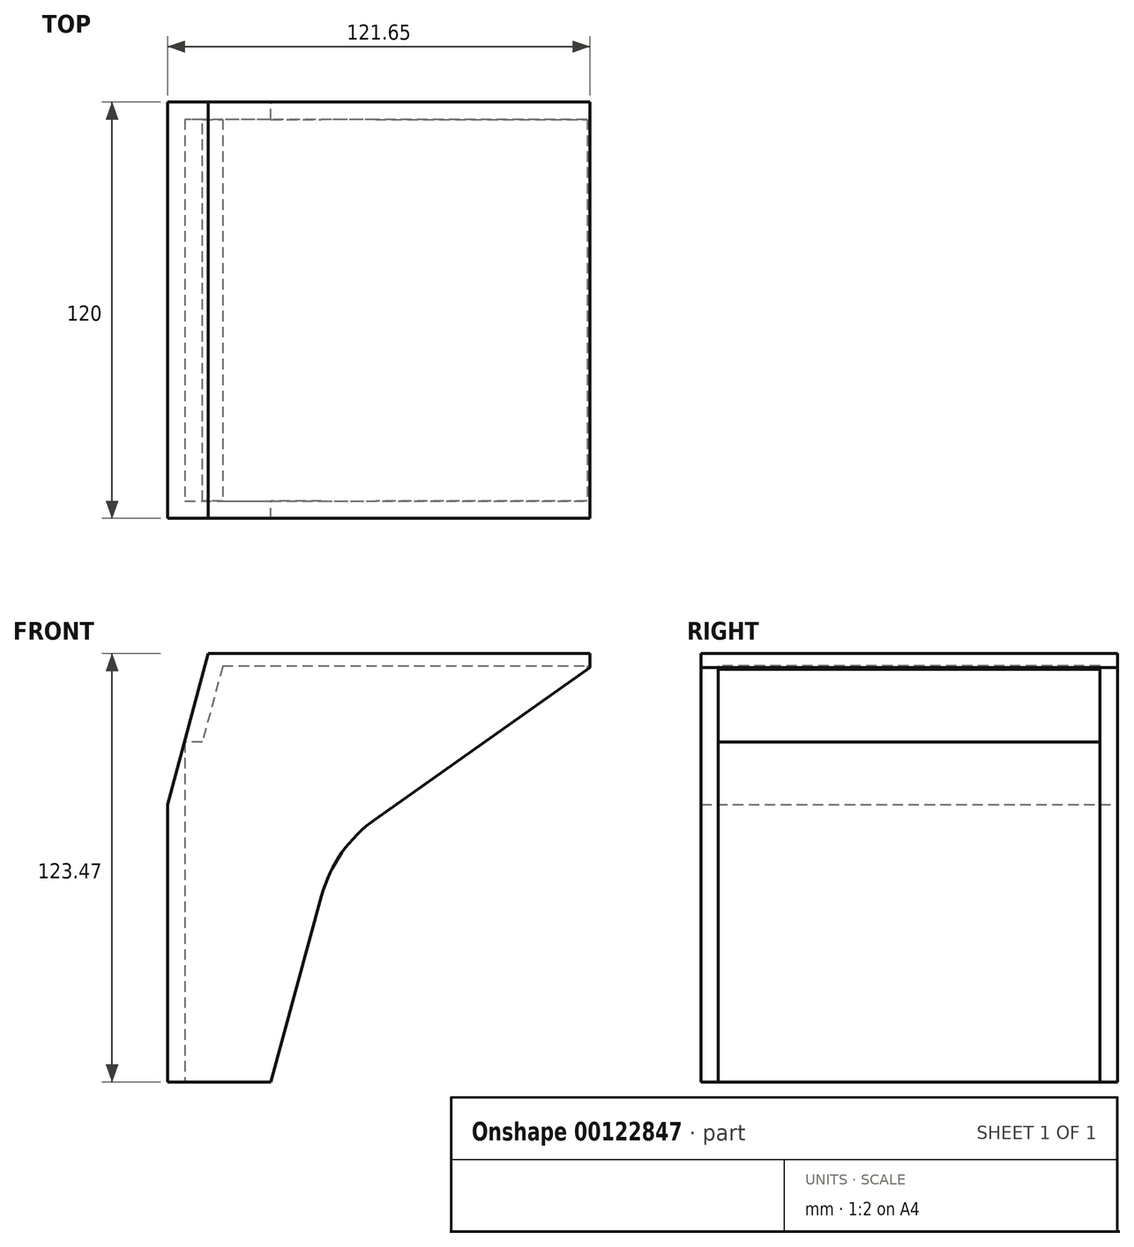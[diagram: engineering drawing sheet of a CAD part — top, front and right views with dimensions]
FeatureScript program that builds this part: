
annotation { "Feature Type Name" : "Feature", "Feature Type Description" : "" }
export const myFeature = defineFeature(function(context is Context, id is Id, definition is map)
    precondition{}
    {
        {
            var Q0;
            Q0=qCreatedBy(makeId("Front.planeOp"),FACE);
            var sketch = newSketch(context, id + "F0", { "sketchPlane" : qUnion([Q0])});
            skLineSegment(sketch, "E0", {"start": v(0, 0) * mm, "end": v(0, 80) * mm});
            skLineSegment(sketch, "E1", {"start": v(0, 80) * mm, "end": v(11.65, 123.47) * mm});
            skLineSegment(sketch, "E2", {"start": v(11.65, 123.47) * mm, "end": v(121.65, 123.47) * mm});
            skLineSegment(sketch, "E3", {"start": v(0, 0) * mm, "end": v(29.72, 0) * mm});
            skLineSegment(sketch, "E4", {"start": v(29.72, 0) * mm, "end": v(44.36, 53.68) * mm});
            skLineSegment(sketch, "E5", {"start": v(121.65, 123.47) * mm, "end": v(121.65, 119.47) * mm});
            skLineSegment(sketch, "E6", {"start": v(59.87, 75.82) * mm, "end": v(121.65, 119.47) * mm});
            skPoint(sketch, "E7.visualSharp", {"position": v(48.14, 67.53) * mm});
            skArc(sketch, "E7.filletArc", {"start": v(59.87, 75.82) * mm, "mid": v(50.2, 66.1) * mm, "end": v(44.36, 53.68) * mm});
            skSolve(sketch);
        }
        {
            var Q0;
            Q0=makeQuery(id+"F0.imprint","IMPRINT",FACE,{"disambiguationData":[TD([[makeQuery(id+"F0.imprint","IMPRINT",EDGE,{"derivedFrom":sQuery(id+"F0.wireOp",EDGE,"E0")}),-1.0]])]});
            extrude(context, id + "F1", {"entities" : qUnion([Q0]), "depth" : 120 * mm});
        }
        {
            var Q0;
            Q0=makeQuery(id+"F1.opExtrude","SWEPT_FACE",FACE,{"disambiguationData":[OSD([sQuery(id+"F0.wireOp",EDGE,"E3")])]});
            var sketch = newSketch(context, id + "F2", { "sketchPlane" : qUnion([Q0])});
            skLineSegment(sketch, "E8.0", {"start": v(0, 120) * mm, "end": v(0, 0) * mm, "construction": true});
            skLineSegment(sketch, "E9", {"start": v(0, 60) * mm, "end": v(5, 60) * mm, "construction": true});
            skLineSegment(sketch, "E10", {"start": v(5, 60) * mm, "end": v(5, 100) * mm});
            skLineSegment(sketch, "E11", {"start": v(5, 100) * mm, "end": v(115, 100) * mm});
            skLineSegment(sketch, "E12", {"start": v(115, 100) * mm, "end": v(115, 20) * mm});
            skLineSegment(sketch, "E13", {"start": v(115, 20) * mm, "end": v(5, 20) * mm});
            skLineSegment(sketch, "E14", {"start": v(5, 20) * mm, "end": v(5, 60) * mm});
            skSolve(sketch);
        }
        {
            var Q0;
            {var subQ0=sQuery(id+"F2.wireOp",EDGE,"E12");Q0=makeQuery(id+"F2.imprint","IMPRINT",FACE,{"disambiguationData":[TD([[makeQuery(id+"F2.imprint","IMPRINT",EDGE,{"derivedFrom":subQ0}),-1.0]])]});}
            var Q1;
            {var subQ5=sQuery(id+"F2.wireOp",EDGE,"E10");Q1=makeQuery(id+"F2.imprint","IMPRINT",FACE,{"disambiguationData":[TD([[makeQuery(id+"F2.imprint","IMPRINT",EDGE,{"derivedFrom":subQ5}),-1.0]])]});}
            extrude(context, id + "F3", {"entities" : qUnion([Q0, Q1]), "operationType" : NewBodyOperationType.REMOVE, "oppositeDirection" : true, "depth" : 98 * mm});
        }
        {
            var Q0;
            Q0=makeQuery(id+"F1.opExtrude","SWEPT_FACE",FACE,{"disambiguationData":[OSD([sQuery(id+"F0.wireOp",EDGE,"E1")])]});
            cPlane(context, id + "F4", {"entities" : qUnion([Q0]), "cplaneType" : CPlaneType.OFFSET, "offset" : 5 * mm, "oppositeDirection" : true, "width" : 150 * mm, "height" : 150 * mm});
        }
        {
            var Q0;
            Q0=qCreatedBy(id+"F4.planeOp",FACE);
            var sketch = newSketch(context, id + "F5", { "sketchPlane" : qUnion([Q0])});
            skLineSegment(sketch, "E15.0", {"start": v(120, 77.27) * mm, "end": v(120, 122.27) * mm, "construction": true});
            skLineSegment(sketch, "E16", {"start": v(120, 99.77) * mm, "end": v(115, 99.77) * mm, "construction": true});
            skLineSegment(sketch, "E17", {"start": v(115, 99.77) * mm, "end": v(115, 119.77) * mm});
            skLineSegment(sketch, "E18", {"start": v(115, 99.77) * mm, "end": v(115, 79.77) * mm});
            skLineSegment(sketch, "E19", {"start": v(115, 79.77) * mm, "end": v(35, 79.77) * mm});
            skLineSegment(sketch, "E20", {"start": v(35, 79.77) * mm, "end": v(35, 119.77) * mm});
            skLineSegment(sketch, "E21", {"start": v(35, 119.77) * mm, "end": v(115, 119.77) * mm});
            skSolve(sketch);
        }
        {
            var Q0;
            Q0 = qSketchRegion(id + "F5", true);
            extrude(context, id + "F6", {"entities" : qUnion([Q0]), "operationType" : NewBodyOperationType.REMOVE, "oppositeDirection" : true, "depth" : 80 * mm});
        }
        {
            var Q0;
            Q0=qCreatedBy(makeId("Top.planeOp"),FACE);
            var sketch = newSketch(context, id + "F7", { "sketchPlane" : qUnion([Q0])});
            skLineSegment(sketch, "E22.0", {"start": v(15.83, -35) * mm, "end": v(15.83, -115) * mm});
            skLineSegment(sketch, "E23", {"start": v(15.83, -115) * mm, "end": v(120.83, -115) * mm});
            skLineSegment(sketch, "E24", {"start": v(120.83, -115) * mm, "end": v(120.83, -35) * mm});
            skLineSegment(sketch, "E25", {"start": v(120.83, -35) * mm, "end": v(15.83, -35) * mm});
            skSolve(sketch);
        }
        {
            var Q0;
            Q0=makeQuery(id+"F7.imprint","IMPRINT",FACE,{"disambiguationData":[TD([[makeQuery(id+"F7.imprint","IMPRINT",EDGE,{"derivedFrom":sQuery(id+"F7.wireOp",EDGE,"E22.0")}),1.0]])]});
            extrude(context, id + "F8", {"entities" : qUnion([Q0]), "operationType" : NewBodyOperationType.REMOVE, "depth" : 120 * mm});
        }
        {
            var Q0;
            Q0=makeQuery(id+"F3.boolean.opBoolean","COPY",FACE,{"derivedFrom":makeQuery(id+"F3.opExtrude","SWEPT_FACE",FACE,{"disambiguationData":[OSD([sQuery(id+"F2.wireOp",EDGE,"E13")])]})});
            extrude(context, id + "F9", {"entities" : qUnion([Q0]), "operationType" : NewBodyOperationType.REMOVE, "oppositeDirection" : true, "depth" : 15 * mm});
        }
        {
            var Q0;
            Q0=makeQuery(id+"F8.boolean.opBoolean","MERGE",FACE,{"derivedFrom":[makeQuery(id+"F6.boolean.opBoolean","COPY",FACE,{"derivedFrom":makeQuery(id+"F6.opExtrude","SWEPT_FACE",FACE,{"disambiguationData":[OSD([sQuery(id+"F5.wireOp",EDGE,"E20")])]})}),makeQuery(id+"F8.opExtrude","SWEPT_FACE",FACE,{"disambiguationData":[OSD([sQuery(id+"F7.wireOp",EDGE,"E25")])]})]});
            extrude(context, id + "F10", {"entities" : qUnion([Q0]), "operationType" : NewBodyOperationType.REMOVE, "oppositeDirection" : true, "depth" : 30 * mm});
        }
        {
            var Q0;
            Q0=makeQuery(id+"F3.boolean.opBoolean","COPY",FACE,{"derivedFrom":makeQuery(id+"F3.opExtrude","SWEPT_FACE",FACE,{"disambiguationData":[OSD([sQuery(id+"F2.wireOp",EDGE,"E11")])]})});
            extrude(context, id + "F11", {"entities" : qUnion([Q0]), "operationType" : NewBodyOperationType.REMOVE, "oppositeDirection" : true, "depth" : 15 * mm});
        }
    });
